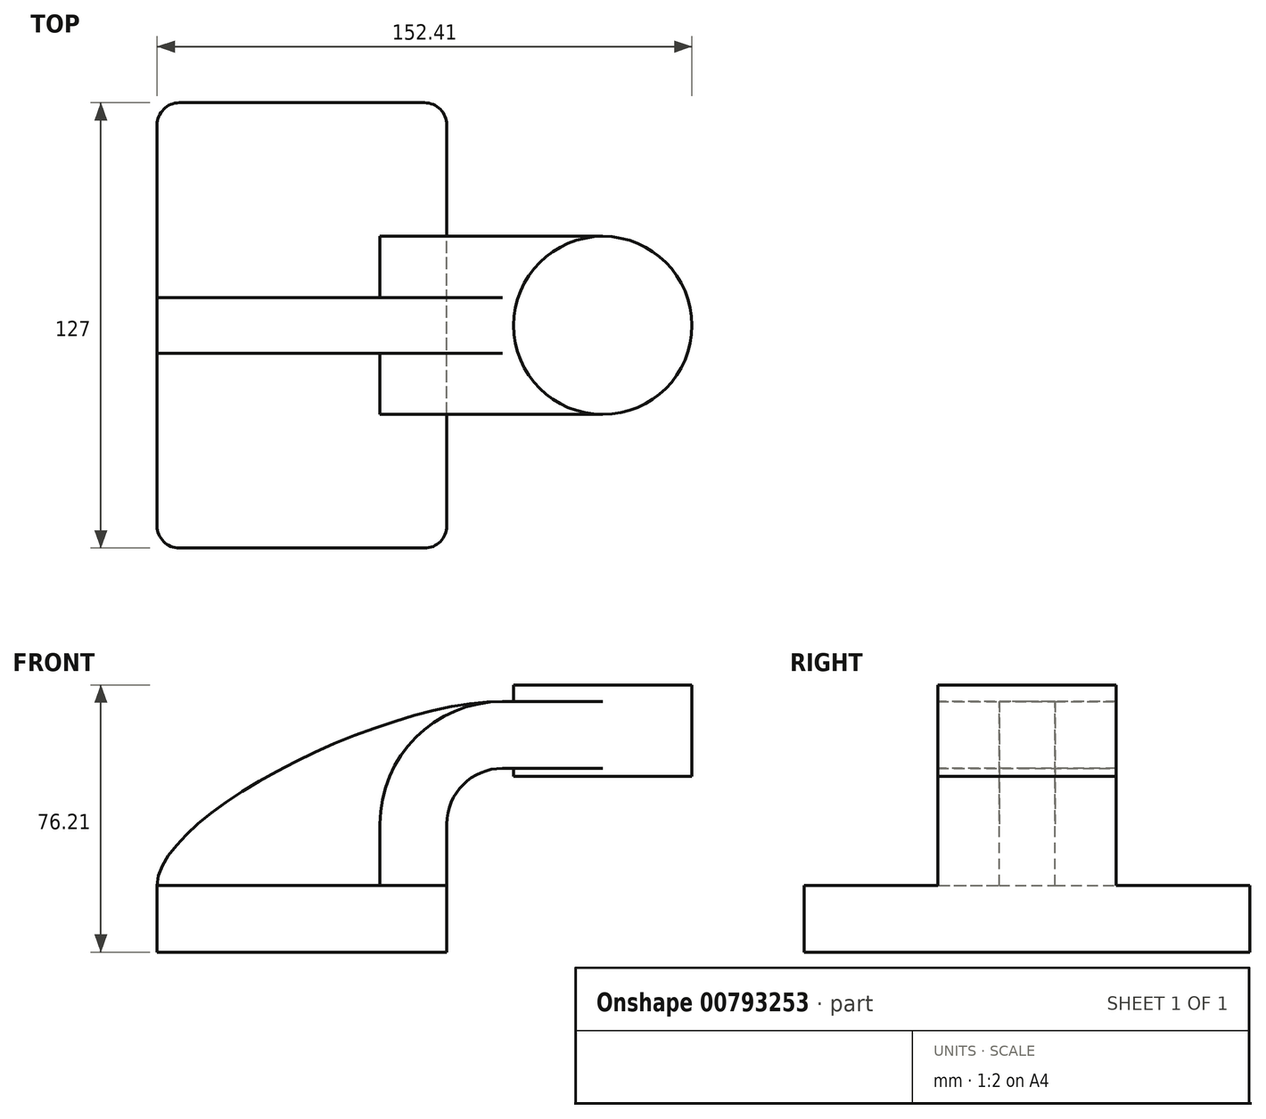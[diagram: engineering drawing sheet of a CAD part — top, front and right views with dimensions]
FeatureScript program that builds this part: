
annotation { "Feature Type Name" : "Feature", "Feature Type Description" : "" }
export const myFeature = defineFeature(function(context is Context, id is Id, definition is map)
    precondition{}
    {
        {
            var Q0;
            Q0=qCreatedBy(makeId("Front.planeOp"),FACE);
            var sketch = newSketch(context, id + "F0", { "sketchPlane" : qUnion([Q0])});
            skLineSegment(sketch, "E0.bottom", {"start": v(41.28, -9.52) * mm, "end": v(-41.28, -9.53) * mm});
            skLineSegment(sketch, "E0.top", {"start": v(41.27, 9.53) * mm, "end": v(-41.28, 9.53) * mm});
            skLineSegment(sketch, "E0.left", {"start": v(41.28, -9.52) * mm, "end": v(41.28, 9.53) * mm});
            skLineSegment(sketch, "E0.right", {"start": v(-41.28, -9.53) * mm, "end": v(-41.28, 9.53) * mm});
            skPoint(sketch, "E0.middle", {"position": v(0, 0) * mm});
            skLineSegment(sketch, "E1.bottom", {"start": v(111.12, 40.64) * mm, "end": v(60.33, 40.64) * mm});
            skLineSegment(sketch, "E1.top", {"start": v(111.12, 66.68) * mm, "end": v(60.33, 66.68) * mm});
            skLineSegment(sketch, "E1.left", {"start": v(111.12, 40.64) * mm, "end": v(111.12, 66.68) * mm});
            skLineSegment(sketch, "E1.right", {"start": v(60.33, 40.64) * mm, "end": v(60.33, 66.68) * mm});
            skPoint(sketch, "E1.middle", {"position": v(85.72, 53.66) * mm});
            skLineSegment(sketch, "E2", {"start": v(41.27, 9.53) * mm, "end": v(41.27, 27) * mm});
            skArc(sketch, "E3", {"start": v(57.15, 42.88) * mm, "mid": v(45.92, 38.23) * mm, "end": v(41.27, 27) * mm});
            skLineSegment(sketch, "E4", {"start": v(57.15, 42.88) * mm, "end": v(85.72, 42.88) * mm});
            skLineSegment(sketch, "E5.0", {"start": v(57.15, 61.93) * mm, "end": v(85.72, 61.93) * mm});
            skArc(sketch, "E5.1", {"start": v(57.15, 61.93) * mm, "mid": v(32.45, 51.7) * mm, "end": v(22.23, 27) * mm});
            skLineSegment(sketch, "E5.2", {"start": v(22.22, 9.53) * mm, "end": v(22.22, 27) * mm});
            skLineSegment(sketch, "E6", {"start": v(85.72, 40.64) * mm, "end": v(85.72, 66.68) * mm});
            skFitSpline(sketch, "E7", {"points": [v(-41.28, 9.52) * mm, v(57.15, 61.93) * mm], "startDerivative": vector(0.97, 60.74) * mm, "endDerivative": vector(100.18, -0.88) * mm});
            skSolve(sketch);
        }
        {
            var Q0;
            Q0=makeQuery(id+"F0.imprint","IMPRINT",FACE,{"disambiguationData":[TD([[makeQuery(id+"F0.imprint","IMPRINT",EDGE,{"derivedFrom":sQuery(id+"F0.wireOp",EDGE,"E0.bottom")}),-1.0]])]});
            extrude(context, id + "F1", {"entities" : qUnion([Q0]), "endBound" : BoundingType.SYMMETRIC, "depth" : 127 * mm, "offsetDistance" : 25.4 * mm});
        }
        {
            var Q0;
            Q0=makeQuery(id+"F0.imprint","IMPRINT",FACE,{"disambiguationData":[TD([[makeQuery(id+"F0.imprint","IMPRINT",EDGE,{"derivedFrom":sQuery(id+"F0.wireOp",EDGE,"E5.1")}),-1.0]])]});
            extrude(context, id + "F2", {"entities" : qUnion([Q0]), "operationType" : NewBodyOperationType.ADD, "endBound" : BoundingType.SYMMETRIC, "depth" : 15.88 * mm, "offsetDistance" : 25.4 * mm});
        }
        {
            var Q0;
            {var subQ1=sQuery(id+"F0.wireOp",EDGE,"E2");Q0=makeQuery(id+"F0.imprint","IMPRINT",FACE,{"disambiguationData":[TD([[makeQuery(id+"F0.imprint","IMPRINT",EDGE,{"derivedFrom":subQ1}),1.0]])]});}
            var Q1;
            {var subQ0=sQuery(id+"F0.wireOp",EDGE,"E4");var subQ1=sQuery(id+"F0.wireOp",EDGE,"E1.right");var subQ2=makeQuery(id+"F0.imprint","INTERSECT",VERTEX,{"derivedFrom":[subQ1,subQ0]});Q1=makeQuery(id+"F0.imprint","IMPRINT",FACE,{"disambiguationData":[TD([[makeQuery(id+"F0.imprint","IMPRINT",EDGE,{"disambiguationData":[TD([[subQ2,-1.0]])],"derivedFrom":subQ1}),-1.0]])]});}
            extrude(context, id + "F3", {"entities" : qUnion([Q0, Q1]), "operationType" : NewBodyOperationType.ADD, "endBound" : BoundingType.SYMMETRIC, "depth" : 50.8 * mm, "offsetDistance" : 25.4 * mm});
        }
        {
            var Q0;
            {var subQ4=sQuery(id+"F0.wireOp",EDGE,"E1.left");Q0=makeQuery(id+"F0.imprint","IMPRINT",FACE,{"disambiguationData":[TD([[makeQuery(id+"F0.imprint","IMPRINT",EDGE,{"derivedFrom":subQ4}),1.0]])]});}
            var Q1;
            Q1=sQuery(id+"F0.wireOp",EDGE,"E6");
            revolve(context, id + "F4", {"operationType" : NewBodyOperationType.ADD, "surfaceOperationType" : NewSurfaceOperationType.NEW, "entities" : qUnion([Q0]), "axis" : qUnion([Q1]), "revolveType" : RevolveType.FULL});
        }
        {
            var Q0;
            Q0=makeQuery(id+"F1.opExtrude","CAP_EDGE",EDGE,{"disambiguationData":[OSD([sQuery(id+"F0.wireOp",EDGE,"E0.left")])],"isStart":false});
            var Q1;
            Q1=makeQuery(id+"F1.opExtrude","CAP_EDGE",EDGE,{"disambiguationData":[OSD([sQuery(id+"F0.wireOp",EDGE,"E0.right")])],"isStart":false});
            var Q2;
            Q2=makeQuery(id+"F1.opExtrude","CAP_EDGE",EDGE,{"disambiguationData":[OSD([sQuery(id+"F0.wireOp",EDGE,"E0.left")])],"isStart":true});
            var Q3;
            Q3=makeQuery(id+"F1.opExtrude","CAP_EDGE",EDGE,{"disambiguationData":[OSD([sQuery(id+"F0.wireOp",EDGE,"E0.right")])],"isStart":true});
            fillet(context, id + "F5", {"entities" : qUnion([Q0, Q1, Q2, Q3]), "radius" : 6.35 * mm, "tangentPropagation" : true, "allowEdgeOverflow" : false});
        }
    });
